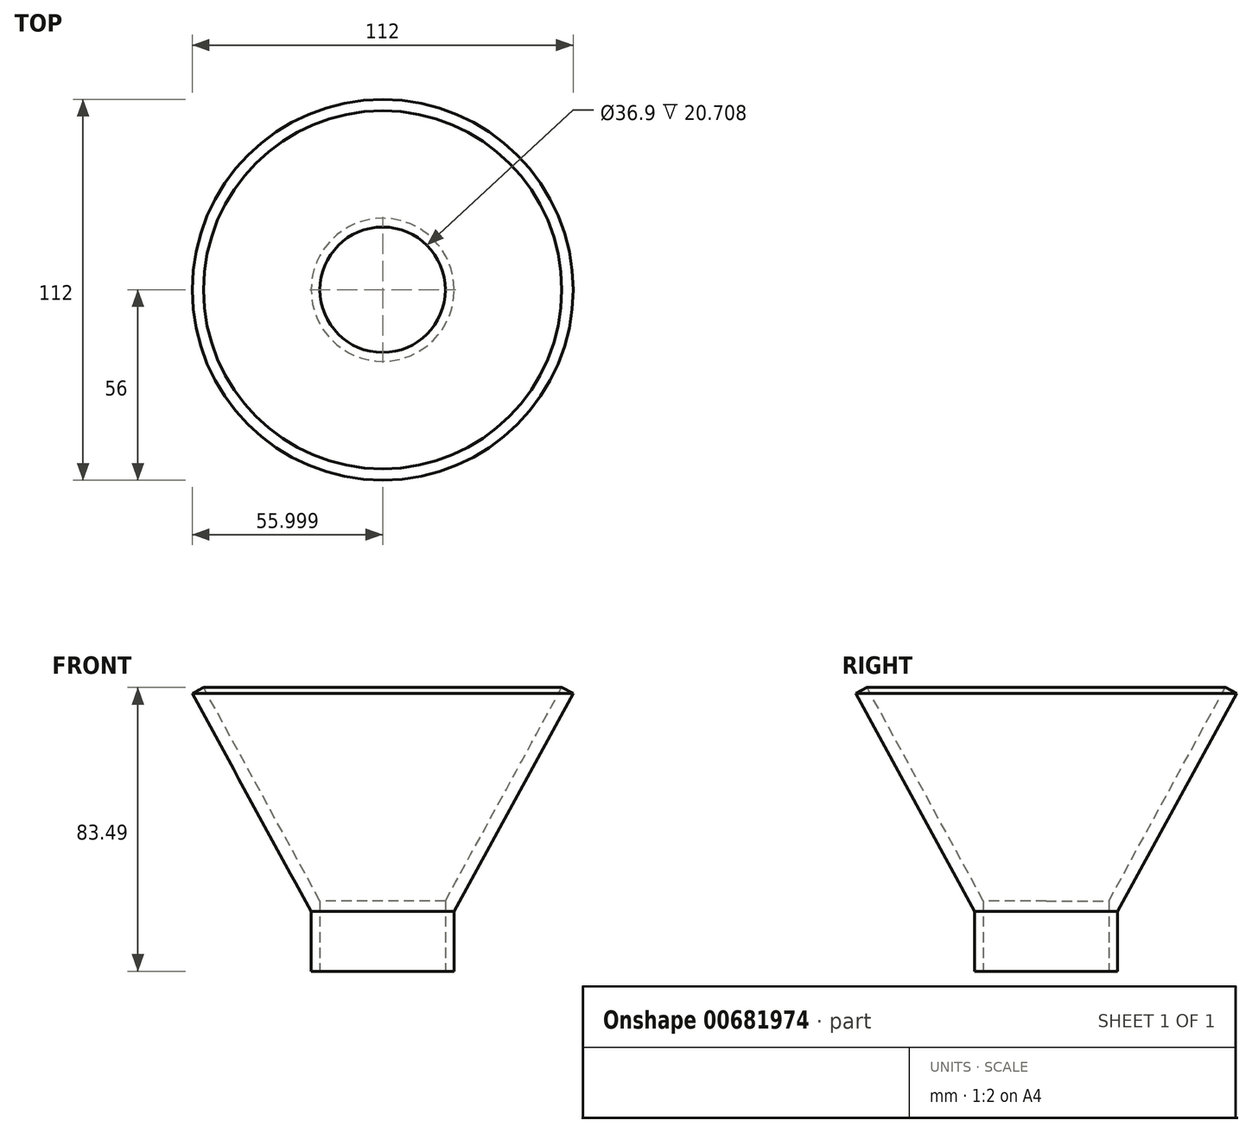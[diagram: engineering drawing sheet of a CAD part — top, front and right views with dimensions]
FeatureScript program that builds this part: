
annotation { "Feature Type Name" : "Feature", "Feature Type Description" : "" }
export const myFeature = defineFeature(function(context is Context, id is Id, definition is map)
    precondition{}
    {
        {
            var Q0;
            Q0=qCreatedBy(makeId("Front.planeOp"),FACE);
            var sketch = newSketch(context, id + "F0", { "sketchPlane" : qUnion([Q0])});
            skLineSegment(sketch, "E0", {"start": v(0.72, 1.33) * mm, "end": v(35.95, 65.93) * mm});
            skLineSegment(sketch, "E1", {"start": v(35.95, 65.93) * mm, "end": v(39.27, 64.12) * mm});
            skLineSegment(sketch, "E2", {"start": v(39.27, 64.12) * mm, "end": v(4.3, 0) * mm});
            skLineSegment(sketch, "E3", {"start": v(4.3, 0) * mm, "end": v(4.3, -17.56) * mm});
            skLineSegment(sketch, "E4", {"start": v(4.3, -17.56) * mm, "end": v(-16.73, -17.56) * mm});
            skLineSegment(sketch, "E5", {"start": v(-16.73, -17.56) * mm, "end": v(-16.73, 1.33) * mm});
            skLineSegment(sketch, "E6", {"start": v(-16.73, 1.33) * mm, "end": v(0.72, 1.33) * mm});
            skSolve(sketch);
        }
        {
            var Q0;
            Q0 = qSketchRegion(id + "F0", true);
            var Q1;
            Q1=sQuery(id+"F0.wireOp",EDGE,"E5");
            revolve(context, id + "F1", {"entities" : qUnion([Q0]), "axis" : qUnion([Q1]), "revolveType" : RevolveType.FULL});
        }
        {
            var Q0;
            Q0=makeQuery(id+"F1.opRevolve","SWEPT_FACE",FACE,{"disambiguationData":[OSD([sQuery(id+"F0.wireOp",EDGE,"E4")])]});
            var sketch = newSketch(context, id + "F2", { "sketchPlane" : qUnion([Q0])});
            skCircle(sketch, "E7", {"center": v(-16.73, 0) * mm, "radius": 18.45 * mm});
            skSolve(sketch);
        }
        {
            var Q0;
            Q0 = qSketchRegion(id + "F2", true);
            extrude(context, id + "F3", {"entities" : qUnion([Q0]), "operationType" : NewBodyOperationType.REMOVE, "oppositeDirection" : true, "depth" : 50.8 * mm, "offsetDistance" : 25.4 * mm});
        }
    });
